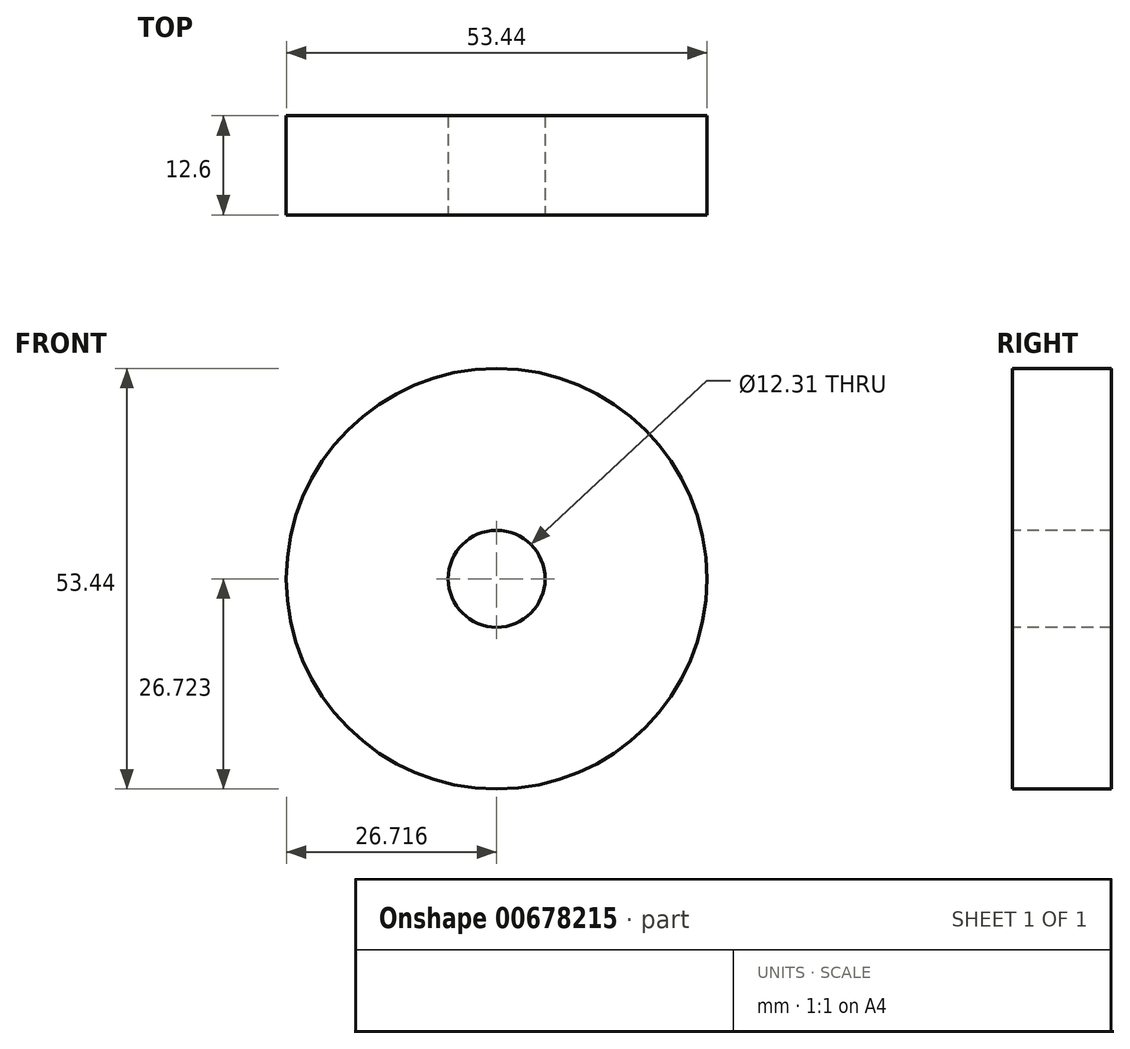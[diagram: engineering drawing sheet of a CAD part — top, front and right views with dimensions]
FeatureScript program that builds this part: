
annotation { "Feature Type Name" : "Feature", "Feature Type Description" : "" }
export const myFeature = defineFeature(function(context is Context, id is Id, definition is map)
    precondition{}
    {
        {
            var Q0;
            Q0=qCreatedBy(makeId("Front.planeOp"),FACE);
            var sketch = newSketch(context, id + "F0", { "sketchPlane" : qUnion([Q0])});
            skCircle(sketch, "E0", {"center": v(6.65, -1.09) * mm, "radius": 26.72 * mm});
            skCircle(sketch, "E1", {"center": v(6.65, -1.09) * mm, "radius": 29.31 * mm, "construction": true});
            skCircle(sketch, "E2", {"center": v(6.65, -1.09) * mm, "radius": 31.75 * mm, "construction": true});
            skLineSegment(sketch, "E3", {"start": v(6.65, -1.09) * mm, "end": v(6.65, 49.12) * mm, "construction": true});
            skLineSegment(sketch, "E4", {"start": v(6.65, -1.09) * mm, "end": v(0.09, 99) * mm, "construction": true});
            skLineSegment(sketch, "E5", {"start": v(6.65, 28.23) * mm, "end": v(-46.15, 28.23) * mm, "construction": true});
            skLineSegment(sketch, "E6", {"start": v(6.65, 28.23) * mm, "end": v(-43.75, 9.88) * mm, "construction": true});
            skCircle(sketch, "E7", {"center": v(6.65, -1.09) * mm, "radius": 27.55 * mm, "construction": true});
            skCircle(sketch, "E8", {"center": v(6.65, 28.23) * mm, "radius": 14.6 * mm, "construction": true});
            skCircle(sketch, "E9", {"center": v(-7.08, 23.23) * mm, "radius": 14.6 * mm, "construction": true});
            skArc(sketch, "E10", {"start": v(6.65, 28.23) * mm, "mid": v(6.13, 29.46) * mm, "end": v(5.5, 30.64) * mm});
            skArc(sketch, "E11", {"start": v(7.33, 25.63) * mm, "mid": v(7.05, 26.94) * mm, "end": v(6.65, 28.23) * mm});
            skArc(sketch, "E12", {"start": v(3.63, 30.52) * mm, "mid": v(4.57, 30.57) * mm, "end": v(5.5, 30.64) * mm});
            skArc(sketch, "E13.MirrorCS", {"start": v(3.01, 30.39) * mm, "mid": v(3.87, 33.04) * mm, "end": v(5.22, 35.48) * mm});
            skArc(sketch, "E14.MirrorCS", {"start": v(2.79, 25.35) * mm, "mid": v(2.68, 27.88) * mm, "end": v(3.01, 30.39) * mm});
            skArc(sketch, "E15.MirrorCS", {"start": v(10.28, 30.39) * mm, "mid": v(9.42, 33.04) * mm, "end": v(8.07, 35.48) * mm});
            skArc(sketch, "E16.MirrorCS", {"start": v(10.5, 25.35) * mm, "mid": v(10.6, 27.88) * mm, "end": v(10.28, 30.39) * mm});
            skArc(sketch, "E17", {"start": v(5.22, 35.48) * mm, "mid": v(6.65, 33.62) * mm, "end": v(8.07, 35.48) * mm});
            skSolve(sketch);
        }
        {
            var Q0;
            Q0=makeQuery(id+"F0.imprint","IMPRINT",FACE,{"disambiguationData":[TD([[makeQuery(id+"F0.imprint","IMPRINT",EDGE,{"derivedFrom":sQuery(id+"F0.wireOp",EDGE,"E13.MirrorCS")}),-1.0]])]});
            var Q1;
            {var subQ0=sQuery(id+"F0.wireOp",EDGE,"E0");var subQ1=makeQuery(id+"F0.imprint","IMPRINT",VERTEX,{"derivedFrom":subQ0});Q1=makeQuery(id+"F0.imprint","IMPRINT",FACE,{"disambiguationData":[TD([[makeQuery(id+"F0.imprint","IMPRINT",EDGE,{"disambiguationData":[TD([[subQ1,1.0]])],"derivedFrom":subQ0}),1.0]])]});}
            extrude(context, id + "F1", {"entities" : qUnion([Q0, Q1]), "depth" : 12.6 * mm, "offsetDistance" : 25 * mm});
        }
        {
            var Q0;
            Q0=makeQuery(id+"F1.opExtrude","SWEPT_BODY",BODY,{"disambiguationData":[OSD([sQuery(id+"F0.wireOp",EDGE,"E0"),sQuery(id+"F0.wireOp",EDGE,"E10"),sQuery(id+"F0.wireOp",EDGE,"E11"),sQuery(id+"F0.wireOp",EDGE,"5612cf1f-b7a4-4f33-bc48-4e26648d2d57.MirrorCS"),sQuery(id+"F0.wireOp",EDGE,"70c40618-e7c3-4c73-ac10-bd37e9988a4a.MirrorCS"),sQuery(id+"F0.wireOp",EDGE,"E12"),sQuery(id+"F0.wireOp",EDGE,"4895722e-1157-4ccf-af4c-292f4bfcae0c")])]});
            var Q1;
            Q1=makeQuery(id+"F1.opExtrude","SWEPT_FACE",FACE,{"disambiguationData":[OSD([sQuery(id+"F0.wireOp",EDGE,"E0")])]});
            circularPattern(context, id + "F2", {"operationType" : NewBodyOperationType.ADD, "entities" : qUnion([Q0]), "axis" : qUnion([Q1]), "angle" : 360 * degree, "instanceCount" : 12, "equalSpace" : true});
        }
        {
            var Q0;
            Q0=makeQuery(id+"F1.opExtrude","CAP_FACE",FACE,{"disambiguationData":[OSD([sQuery(id+"F0.wireOp",EDGE,"E0"),sQuery(id+"F0.wireOp",EDGE,"E13.MirrorCS"),sQuery(id+"F0.wireOp",EDGE,"E14.MirrorCS"),sQuery(id+"F0.wireOp",EDGE,"E15.MirrorCS"),sQuery(id+"F0.wireOp",EDGE,"E16.MirrorCS"),sQuery(id+"F0.wireOp",EDGE,"E17")])],"isStart":false});
            var sketch = newSketch(context, id + "F3", { "sketchPlane" : qUnion([Q0])});
            skCircle(sketch, "E18", {"center": v(6.65, -1.09) * mm, "radius": 6.15 * mm});
            skSolve(sketch);
        }
        {
            var Q0;
            Q0 = qSketchRegion(id + "F3", true);
            extrude(context, id + "F4", {"entities" : qUnion([Q0]), "operationType" : NewBodyOperationType.REMOVE, "oppositeDirection" : true, "depth" : 25 * mm, "offsetDistance" : 25 * mm});
        }
    });
